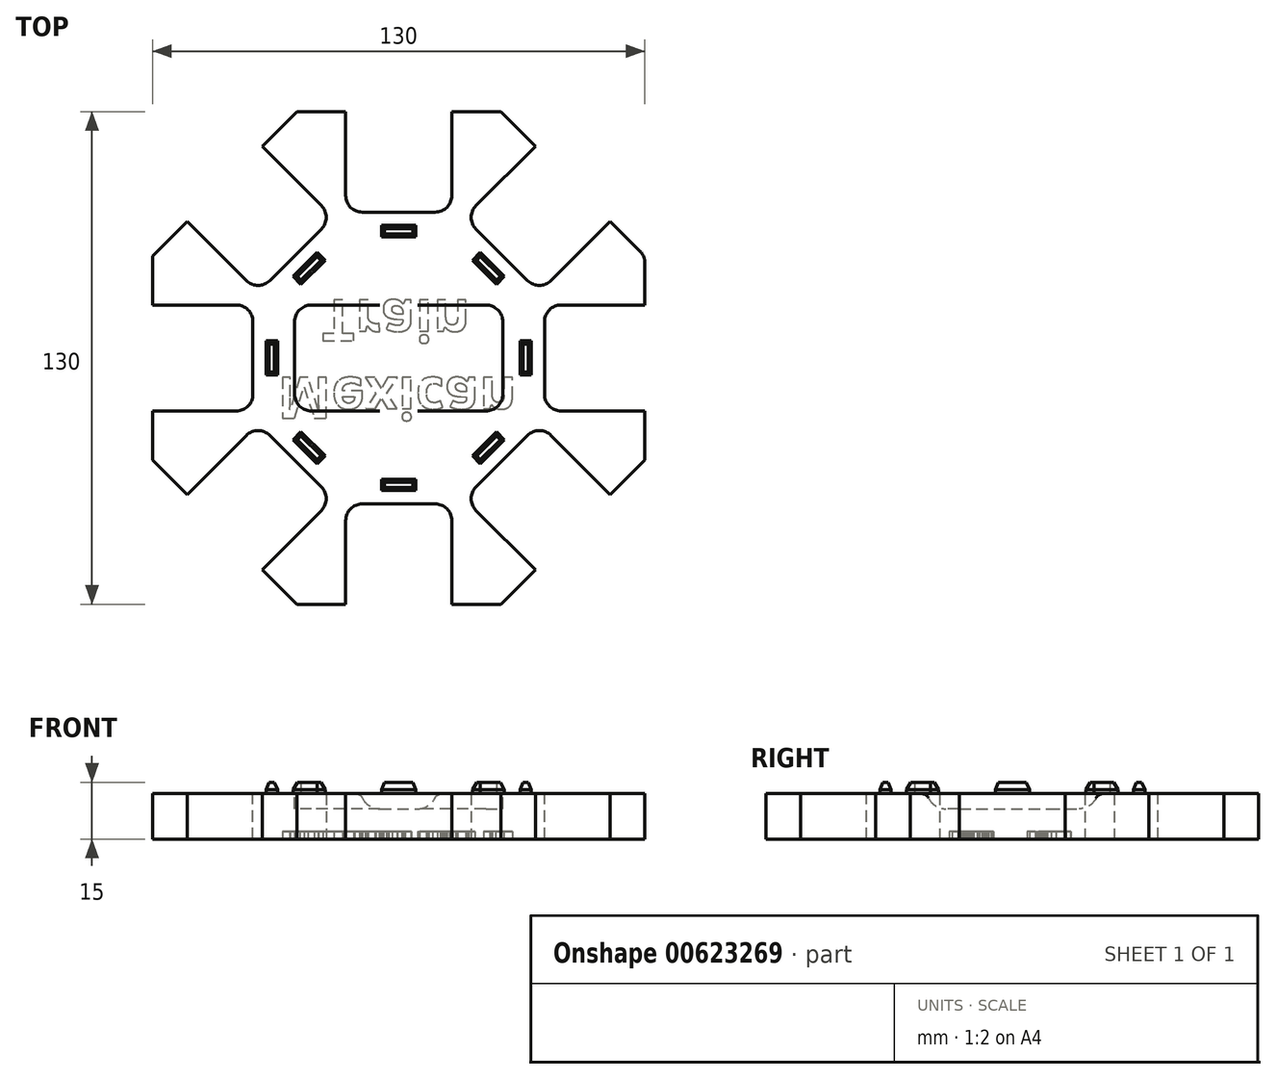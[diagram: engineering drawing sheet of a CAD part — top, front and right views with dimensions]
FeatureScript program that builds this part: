
annotation { "Feature Type Name" : "Feature", "Feature Type Description" : "" }
export const myFeature = defineFeature(function(context is Context, id is Id, definition is map)
    precondition{}
    {
        {
            var Q0;
            Q0=qCreatedBy(makeId("Top.planeOp"),FACE);
            var sketch = newSketch(context, id + "F0", { "sketchPlane" : qUnion([Q0])});
            skCircle(sketch, "E0.cCircle", {"center": v(0, 0) * mm, "radius": 65 * mm, "construction": true});
            skLineSegment(sketch, "E0.0", {"start": v(65, -26.92) * mm, "end": v(26.92, -65) * mm});
            skLineSegment(sketch, "E0.1", {"start": v(26.92, -65) * mm, "end": v(-26.92, -65) * mm});
            skLineSegment(sketch, "E0.2", {"start": v(-26.92, -65) * mm, "end": v(-65, -26.92) * mm});
            skLineSegment(sketch, "E0.3", {"start": v(-65, -26.92) * mm, "end": v(-65, 26.92) * mm});
            skLineSegment(sketch, "E0.4", {"start": v(-65, 26.92) * mm, "end": v(-26.92, 65) * mm});
            skLineSegment(sketch, "E0.5", {"start": v(-26.92, 65) * mm, "end": v(26.92, 65) * mm});
            skLineSegment(sketch, "E0.6", {"start": v(26.92, 65) * mm, "end": v(65, 26.92) * mm});
            skLineSegment(sketch, "E0.7", {"start": v(65, 26.92) * mm, "end": v(65, -26.92) * mm});
            skPoint(sketch, "E0.0.midPoint", {"position": v(45.96, -45.96) * mm});
            skLineSegment(sketch, "E1", {"start": v(0, 65) * mm, "end": v(0, 51.75) * mm, "construction": true});
            skLineSegment(sketch, "E2.bottom", {"start": v(-14, 65) * mm, "end": v(14, 65) * mm});
            skLineSegment(sketch, "E2.top", {"start": v(-14, 38.5) * mm, "end": v(14, 38.5) * mm});
            skLineSegment(sketch, "E2.left", {"start": v(-14, 65) * mm, "end": v(-14, 38.5) * mm});
            skLineSegment(sketch, "E2.right", {"start": v(14, 65) * mm, "end": v(14, 38.5) * mm});
            skPoint(sketch, "E2.middle", {"position": v(0, 51.75) * mm});
            skSolve(sketch);
        }
        {
            var Q0;
            Q0=makeQuery(id+"F0.imprint","IMPRINT",FACE,{"disambiguationData":[TD([[makeQuery(id+"F0.imprint","IMPRINT",EDGE,{"derivedFrom":sQuery(id+"F0.wireOp",EDGE,"E0.0")}),-1.0]])]});
            var Q1;
            Q1=makeQuery(id+"F0.imprint","IMPRINT",FACE,{"disambiguationData":[TD([[makeQuery(id+"F0.imprint","IMPRINT",EDGE,{"derivedFrom":sQuery(id+"F0.wireOp",EDGE,"E2.top")}),1.0]])]});
            extrude(context, id + "F1", {"entities" : qUnion([Q0, Q1]), "depth" : 12 * mm, "offsetDistance" : 25 * mm});
        }
        {
            var Q0;
            Q0=makeQuery(id+"F1.opExtrude","CAP_FACE",FACE,{"disambiguationData":[OSD([sQuery(id+"F0.wireOp",EDGE,"E0.0"),sQuery(id+"F0.wireOp",EDGE,"E0.1"),sQuery(id+"F0.wireOp",EDGE,"E0.2"),sQuery(id+"F0.wireOp",EDGE,"E0.3"),sQuery(id+"F0.wireOp",EDGE,"E0.4"),sQuery(id+"F0.wireOp",EDGE,"E0.5"),sQuery(id+"F0.wireOp",EDGE,"E0.6"),sQuery(id+"F0.wireOp",EDGE,"E0.7"),sQuery(id+"F0.wireOp",EDGE,"E2.bottom")])],"isStart":false});
            var sketch = newSketch(context, id + "F2", { "sketchPlane" : qUnion([Q0])});
            skLineSegment(sketch, "E3", {"start": v(0, 65) * mm, "end": v(0, 51.75) * mm, "construction": true});
            skLineSegment(sketch, "E4.bottom", {"start": v(14, 65) * mm, "end": v(-14, 65) * mm});
            skLineSegment(sketch, "E4.top", {"start": v(14, 38.5) * mm, "end": v(-14, 38.5) * mm});
            skLineSegment(sketch, "E4.left", {"start": v(14, 65) * mm, "end": v(14, 38.5) * mm});
            skLineSegment(sketch, "E4.right", {"start": v(-14, 65) * mm, "end": v(-14, 38.5) * mm});
            skPoint(sketch, "E4.middle", {"position": v(0, 51.75) * mm});
            skLineSegment(sketch, "E5.1.0", {"start": v(-55.86, 36.06) * mm, "end": v(-37.12, 17.32) * mm});
            skLineSegment(sketch, "E5.1.1", {"start": v(-36.06, 55.86) * mm, "end": v(-17.32, 37.12) * mm});
            skLineSegment(sketch, "E5.1.2", {"start": v(-17.32, 37.12) * mm, "end": v(-37.12, 17.32) * mm});
            skLineSegment(sketch, "E5.2.0", {"start": v(-65, -14) * mm, "end": v(-38.5, -14) * mm});
            skLineSegment(sketch, "E5.2.1", {"start": v(-65, 14) * mm, "end": v(-38.5, 14) * mm});
            skLineSegment(sketch, "E5.2.2", {"start": v(-38.5, 14) * mm, "end": v(-38.5, -14) * mm});
            skLineSegment(sketch, "E5.3.0", {"start": v(-36.06, -55.86) * mm, "end": v(-17.32, -37.12) * mm});
            skLineSegment(sketch, "E5.3.1", {"start": v(-55.86, -36.06) * mm, "end": v(-37.12, -17.32) * mm});
            skLineSegment(sketch, "E5.3.2", {"start": v(-37.12, -17.32) * mm, "end": v(-17.32, -37.12) * mm});
            skLineSegment(sketch, "E5.4.0", {"start": v(14, -65) * mm, "end": v(14, -38.5) * mm});
            skLineSegment(sketch, "E5.4.1", {"start": v(-14, -65) * mm, "end": v(-14, -38.5) * mm});
            skLineSegment(sketch, "E5.4.2", {"start": v(-14, -38.5) * mm, "end": v(14, -38.5) * mm});
            skLineSegment(sketch, "E5.5.0", {"start": v(55.86, -36.06) * mm, "end": v(37.12, -17.32) * mm});
            skLineSegment(sketch, "E5.5.1", {"start": v(36.06, -55.86) * mm, "end": v(17.32, -37.12) * mm});
            skLineSegment(sketch, "E5.5.2", {"start": v(17.32, -37.12) * mm, "end": v(37.12, -17.32) * mm});
            skLineSegment(sketch, "E5.6.0", {"start": v(65, 14) * mm, "end": v(38.5, 14) * mm});
            skLineSegment(sketch, "E5.6.1", {"start": v(65, -14) * mm, "end": v(38.5, -14) * mm});
            skLineSegment(sketch, "E5.6.2", {"start": v(38.5, -14) * mm, "end": v(38.5, 14) * mm});
            skLineSegment(sketch, "E5.7.0", {"start": v(36.06, 55.86) * mm, "end": v(17.32, 37.12) * mm});
            skLineSegment(sketch, "E5.7.1", {"start": v(55.86, 36.06) * mm, "end": v(37.12, 17.32) * mm});
            skLineSegment(sketch, "E5.7.2", {"start": v(37.12, 17.32) * mm, "end": v(17.32, 37.12) * mm});
            skPoint(sketch, "E5.center", {"position": v(0, 0) * mm});
            skLineSegment(sketch, "E6.bottom", {"start": v(27.5, -14) * mm, "end": v(-27.5, -14) * mm});
            skLineSegment(sketch, "E6.top", {"start": v(27.5, 14) * mm, "end": v(-27.5, 14) * mm});
            skLineSegment(sketch, "E6.left", {"start": v(27.5, -14) * mm, "end": v(27.5, 14) * mm});
            skLineSegment(sketch, "E6.right", {"start": v(-27.5, -14) * mm, "end": v(-27.5, 14) * mm});
            skLineSegment(sketch, "E7", {"start": v(0, 14) * mm, "end": v(0, -14) * mm});
            skSolve(sketch);
        }
        {
            var Q0;
            Q0=makeQuery(id+"F2.imprint","IMPRINT",FACE,{"disambiguationData":[TD([[makeQuery(id+"F2.imprint","IMPRINT",EDGE,{"derivedFrom":sQuery(id+"F2.wireOp",EDGE,"E4.bottom")}),-1.0]])]});
            var Q1;
            {var subQ0=sQuery(id+"F2.wireOp",EDGE,"E5.1.0");Q1=makeQuery(id+"F2.imprint","IMPRINT",FACE,{"disambiguationData":[TD([[makeQuery(id+"F2.imprint","IMPRINT",EDGE,{"derivedFrom":subQ0}),1.0]])]});}
            var Q2;
            {var subQ0=sQuery(id+"F2.wireOp",EDGE,"E5.2.0");Q2=makeQuery(id+"F2.imprint","IMPRINT",FACE,{"disambiguationData":[TD([[makeQuery(id+"F2.imprint","IMPRINT",EDGE,{"derivedFrom":subQ0}),1.0]])]});}
            var Q3;
            {var subQ0=sQuery(id+"F2.wireOp",EDGE,"E5.7.0");Q3=makeQuery(id+"F2.imprint","IMPRINT",FACE,{"disambiguationData":[TD([[makeQuery(id+"F2.imprint","IMPRINT",EDGE,{"derivedFrom":subQ0}),1.0]])]});}
            var Q4;
            {var subQ0=sQuery(id+"F2.wireOp",EDGE,"E5.6.0");Q4=makeQuery(id+"F2.imprint","IMPRINT",FACE,{"disambiguationData":[TD([[makeQuery(id+"F2.imprint","IMPRINT",EDGE,{"derivedFrom":subQ0}),1.0]])]});}
            var Q5;
            {var subQ0=sQuery(id+"F2.wireOp",EDGE,"E5.5.0");Q5=makeQuery(id+"F2.imprint","IMPRINT",FACE,{"disambiguationData":[TD([[makeQuery(id+"F2.imprint","IMPRINT",EDGE,{"derivedFrom":subQ0}),1.0]])]});}
            var Q6;
            {var subQ0=sQuery(id+"F2.wireOp",EDGE,"E5.4.0");Q6=makeQuery(id+"F2.imprint","IMPRINT",FACE,{"disambiguationData":[TD([[makeQuery(id+"F2.imprint","IMPRINT",EDGE,{"derivedFrom":subQ0}),1.0]])]});}
            var Q7;
            {var subQ0=sQuery(id+"F2.wireOp",EDGE,"E5.3.0");Q7=makeQuery(id+"F2.imprint","IMPRINT",FACE,{"disambiguationData":[TD([[makeQuery(id+"F2.imprint","IMPRINT",EDGE,{"derivedFrom":subQ0}),1.0]])]});}
            extrude(context, id + "F3", {"entities" : qUnion([Q0, Q1, Q2, Q3, Q4, Q5, Q6, Q7]), "operationType" : NewBodyOperationType.REMOVE, "oppositeDirection" : true, "depth" : 25 * mm, "offsetDistance" : 25 * mm});
        }
        {
            var Q0;
            Q0=makeQuery(id+"F3.boolean.opBoolean","COPY",EDGE,{"derivedFrom":makeQuery(id+"F3.opExtrude","SWEPT_EDGE",EDGE,{"disambiguationData":[OSD([sQuery(id+"F2.wireOp",EDGE,"E4.top"),sQuery(id+"F2.wireOp",EDGE,"E4.right")])]})});
            var Q1;
            Q1=makeQuery(id+"F3.boolean.opBoolean","COPY",EDGE,{"derivedFrom":makeQuery(id+"F3.opExtrude","SWEPT_EDGE",EDGE,{"disambiguationData":[OSD([sQuery(id+"F2.wireOp",EDGE,"E5.7.0"),sQuery(id+"F2.wireOp",EDGE,"E5.7.2")])]})});
            var Q2;
            Q2=makeQuery(id+"F3.boolean.opBoolean","COPY",EDGE,{"derivedFrom":makeQuery(id+"F3.opExtrude","SWEPT_EDGE",EDGE,{"disambiguationData":[OSD([sQuery(id+"F2.wireOp",EDGE,"E5.6.0"),sQuery(id+"F2.wireOp",EDGE,"E5.6.2")])]})});
            var Q3;
            Q3=makeQuery(id+"F3.boolean.opBoolean","COPY",EDGE,{"derivedFrom":makeQuery(id+"F3.opExtrude","SWEPT_EDGE",EDGE,{"disambiguationData":[OSD([sQuery(id+"F2.wireOp",EDGE,"E5.5.0"),sQuery(id+"F2.wireOp",EDGE,"E5.5.2")])]})});
            var Q4;
            Q4=makeQuery(id+"F3.boolean.opBoolean","COPY",EDGE,{"derivedFrom":makeQuery(id+"F3.opExtrude","SWEPT_EDGE",EDGE,{"disambiguationData":[OSD([sQuery(id+"F2.wireOp",EDGE,"E5.4.0"),sQuery(id+"F2.wireOp",EDGE,"E5.4.2")])]})});
            var Q5;
            Q5=makeQuery(id+"F3.boolean.opBoolean","COPY",EDGE,{"derivedFrom":makeQuery(id+"F3.opExtrude","SWEPT_EDGE",EDGE,{"disambiguationData":[OSD([sQuery(id+"F2.wireOp",EDGE,"E5.3.0"),sQuery(id+"F2.wireOp",EDGE,"E5.3.2")])]})});
            var Q6;
            Q6=makeQuery(id+"F3.boolean.opBoolean","COPY",EDGE,{"derivedFrom":makeQuery(id+"F3.opExtrude","SWEPT_EDGE",EDGE,{"disambiguationData":[OSD([sQuery(id+"F2.wireOp",EDGE,"E5.2.0"),sQuery(id+"F2.wireOp",EDGE,"E5.2.2")])]})});
            var Q7;
            Q7=makeQuery(id+"F3.boolean.opBoolean","COPY",EDGE,{"derivedFrom":makeQuery(id+"F3.opExtrude","SWEPT_EDGE",EDGE,{"disambiguationData":[OSD([sQuery(id+"F2.wireOp",EDGE,"E5.1.0"),sQuery(id+"F2.wireOp",EDGE,"E5.1.2")])]})});
            var Q8;
            Q8=makeQuery(id+"F3.boolean.opBoolean","COPY",EDGE,{"derivedFrom":makeQuery(id+"F3.opExtrude","SWEPT_EDGE",EDGE,{"disambiguationData":[OSD([sQuery(id+"F2.wireOp",EDGE,"E5.7.1"),sQuery(id+"F2.wireOp",EDGE,"E5.7.2")])]})});
            var Q9;
            Q9=makeQuery(id+"F1.opExtrude","SWEPT_EDGE",EDGE,{"disambiguationData":[OSD([sQuery(id+"F0.wireOp",EDGE,"E0.6"),sQuery(id+"F0.wireOp",EDGE,"E0.7")])]});
            var Q10;
            Q10=makeQuery(id+"F3.boolean.opBoolean","COPY",EDGE,{"derivedFrom":makeQuery(id+"F3.opExtrude","SWEPT_EDGE",EDGE,{"disambiguationData":[OSD([sQuery(id+"F2.wireOp",EDGE,"E5.6.1"),sQuery(id+"F2.wireOp",EDGE,"E5.6.2")])]})});
            var Q11;
            Q11=makeQuery(id+"F3.boolean.opBoolean","COPY",EDGE,{"derivedFrom":makeQuery(id+"F3.opExtrude","SWEPT_EDGE",EDGE,{"disambiguationData":[OSD([sQuery(id+"F2.wireOp",EDGE,"E5.5.1"),sQuery(id+"F2.wireOp",EDGE,"E5.5.2")])]})});
            var Q12;
            Q12=makeQuery(id+"F3.boolean.opBoolean","COPY",EDGE,{"derivedFrom":makeQuery(id+"F3.opExtrude","SWEPT_EDGE",EDGE,{"disambiguationData":[OSD([sQuery(id+"F2.wireOp",EDGE,"E5.4.1"),sQuery(id+"F2.wireOp",EDGE,"E5.4.2")])]})});
            var Q13;
            Q13=makeQuery(id+"F3.boolean.opBoolean","COPY",EDGE,{"derivedFrom":makeQuery(id+"F3.opExtrude","SWEPT_EDGE",EDGE,{"disambiguationData":[OSD([sQuery(id+"F2.wireOp",EDGE,"E5.3.1"),sQuery(id+"F2.wireOp",EDGE,"E5.3.2")])]})});
            var Q14;
            Q14=makeQuery(id+"F3.boolean.opBoolean","COPY",EDGE,{"derivedFrom":makeQuery(id+"F3.opExtrude","SWEPT_EDGE",EDGE,{"disambiguationData":[OSD([sQuery(id+"F2.wireOp",EDGE,"E5.2.1"),sQuery(id+"F2.wireOp",EDGE,"E5.2.2")])]})});
            var Q15;
            Q15=makeQuery(id+"F3.boolean.opBoolean","COPY",EDGE,{"derivedFrom":makeQuery(id+"F3.opExtrude","SWEPT_EDGE",EDGE,{"disambiguationData":[OSD([sQuery(id+"F2.wireOp",EDGE,"E5.1.1"),sQuery(id+"F2.wireOp",EDGE,"E5.1.2")])]})});
            var Q16;
            Q16=makeQuery(id+"F3.boolean.opBoolean","COPY",EDGE,{"derivedFrom":makeQuery(id+"F3.opExtrude","SWEPT_EDGE",EDGE,{"disambiguationData":[OSD([sQuery(id+"F2.wireOp",EDGE,"E4.top"),sQuery(id+"F2.wireOp",EDGE,"E4.left")])]})});
            fillet(context, id + "F4", {"entities" : qUnion([Q0, Q1, Q2, Q3, Q4, Q5, Q6, Q7, Q8, Q9, Q10, Q11, Q12, Q13, Q14, Q15, Q16]), "radius" : 4.4 * mm, "tangentPropagation" : true, "allowEdgeOverflow" : false});
        }
        {
            var Q0;
            Q0=makeQuery(id+"F2.imprint","IMPRINT",FACE,{"disambiguationData":[TD([[makeQuery(id+"F2.imprint","IMPRINT",EDGE,{"derivedFrom":sQuery(id+"F2.wireOp",EDGE,"E6.bottom")}),-1.0]])]});
            extrude(context, id + "F5", {"entities" : qUnion([Q0]), "operationType" : NewBodyOperationType.REMOVE, "oppositeDirection" : true, "depth" : 4 * mm, "offsetDistance" : 25 * mm});
        }
        {
            var Q0;
            Q0=makeQuery(id+"F1.opExtrude","CAP_FACE",FACE,{"disambiguationData":[OSD([sQuery(id+"F0.wireOp",EDGE,"E0.0"),sQuery(id+"F0.wireOp",EDGE,"E0.1"),sQuery(id+"F0.wireOp",EDGE,"E0.2"),sQuery(id+"F0.wireOp",EDGE,"E0.3"),sQuery(id+"F0.wireOp",EDGE,"E0.4"),sQuery(id+"F0.wireOp",EDGE,"E0.5"),sQuery(id+"F0.wireOp",EDGE,"E0.6"),sQuery(id+"F0.wireOp",EDGE,"E0.7")])],"isStart":false});
            var sketch = newSketch(context, id + "F6", { "sketchPlane" : qUnion([Q0])});
            skLineSegment(sketch, "E8", {"start": v(0, 38.5) * mm, "end": v(0, 33.5) * mm, "construction": true});
            skPoint(sketch, "E9.middle", {"position": v(0, 33.5) * mm});
            skLineSegment(sketch, "E10.bottom", {"start": v(4.5, 32) * mm, "end": v(-4.5, 32) * mm});
            skLineSegment(sketch, "E10.top", {"start": v(4.5, 35) * mm, "end": v(-4.5, 35) * mm});
            skLineSegment(sketch, "E10.left", {"start": v(4.5, 32) * mm, "end": v(4.5, 35) * mm});
            skLineSegment(sketch, "E10.right", {"start": v(-4.5, 32) * mm, "end": v(-4.5, 35) * mm});
            skSolve(sketch);
        }
        {
            var Q0;
            {var subQ0=sQuery(id+"F6.wireOp",EDGE,"E9.bottom");Q0=makeQuery(id+"F6.imprint","IMPRINT",FACE,{"disambiguationData":[TD([[makeQuery(id+"F6.imprint","IMPRINT",EDGE,{"derivedFrom":subQ0}),-1.0]])]});}
            var Q1;
            {var subQ5=sQuery(id+"F6.wireOp",EDGE,"E10.left");Q1=makeQuery(id+"F6.imprint","IMPRINT",FACE,{"disambiguationData":[TD([[makeQuery(id+"F6.imprint","IMPRINT",EDGE,{"derivedFrom":subQ5}),1.0]])]});}
            var Q2;
            {var subQ0=sQuery(id+"F6.wireOp",EDGE,"E10.bottom");var subQ1=sQuery(id+"F6.wireOp",EDGE,"E9.left");var subQ2=makeQuery(id+"F6.imprint","INTERSECT",VERTEX,{"derivedFrom":[subQ1,subQ0]});Q2=makeQuery(id+"F6.imprint","IMPRINT",FACE,{"disambiguationData":[TD([[makeQuery(id+"F6.imprint","IMPRINT",EDGE,{"disambiguationData":[TD([[subQ2,-1.0]])],"derivedFrom":subQ1}),1.0]])]});}
            var Q3;
            {var subQ0=sQuery(id+"F6.wireOp",EDGE,"E9.top");Q3=makeQuery(id+"F6.imprint","IMPRINT",FACE,{"disambiguationData":[TD([[makeQuery(id+"F6.imprint","IMPRINT",EDGE,{"derivedFrom":subQ0}),1.0]])]});}
            var Q4;
            {var subQ5=sQuery(id+"F6.wireOp",EDGE,"E10.right");Q4=makeQuery(id+"F6.imprint","IMPRINT",FACE,{"disambiguationData":[TD([[makeQuery(id+"F6.imprint","IMPRINT",EDGE,{"derivedFrom":subQ5}),-1.0]])]});}
            extrude(context, id + "F7", {"entities" : qUnion([Q0, Q1, Q2, Q3, Q4]), "depth" : 3 * mm, "offsetDistance" : 25 * mm});
        }
        {
            var Q0;
            Q0=makeQuery(id+"F1.opExtrude","CAP_FACE",FACE,{"disambiguationData":[OSD([sQuery(id+"F0.wireOp",EDGE,"E0.0"),sQuery(id+"F0.wireOp",EDGE,"E0.1"),sQuery(id+"F0.wireOp",EDGE,"E0.2"),sQuery(id+"F0.wireOp",EDGE,"E0.3"),sQuery(id+"F0.wireOp",EDGE,"E0.4"),sQuery(id+"F0.wireOp",EDGE,"E0.5"),sQuery(id+"F0.wireOp",EDGE,"E0.6"),sQuery(id+"F0.wireOp",EDGE,"E0.7")])],"isStart":false});
            var sketch = newSketch(context, id + "F8", { "sketchPlane" : qUnion([Q0])});
            skPoint(sketch, "E11", {"position": v(0, 0) * mm});
            skCircle(sketch, "E12", {"center": v(0, 0) * mm, "radius": 38.5 * mm, "construction": true});
            skSolve(sketch);
        }
        {
            var Q0;
            Q0=makeQuery(id+"F7.opExtrude","SWEPT_BODY",BODY,{"disambiguationData":[OSD([sQuery(id+"F6.wireOp",EDGE,"E9.bottom"),sQuery(id+"F6.wireOp",EDGE,"E9.top"),sQuery(id+"F6.wireOp",EDGE,"E9.left"),sQuery(id+"F6.wireOp",EDGE,"E9.right"),sQuery(id+"F6.wireOp",EDGE,"E10.bottom"),sQuery(id+"F6.wireOp",EDGE,"E10.top"),sQuery(id+"F6.wireOp",EDGE,"E10.left"),sQuery(id+"F6.wireOp",EDGE,"E10.right")])]});
            var Q1;
            Q1=sQuery(id+"F8.wireOp",EDGE,"E12");
            circularPattern(context, id + "F9", {"entities" : qUnion([Q0]), "axis" : qUnion([Q1]), "angle" : 360 * degree, "instanceCount" : 8, "equalSpace" : true});
        }
        {
            var Q0;
            Q0=makeQuery(id+"F1.opExtrude","CAP_FACE",FACE,{"disambiguationData":[OSD([sQuery(id+"F0.wireOp",EDGE,"E0.0"),sQuery(id+"F0.wireOp",EDGE,"E0.1"),sQuery(id+"F0.wireOp",EDGE,"E0.2"),sQuery(id+"F0.wireOp",EDGE,"E0.3"),sQuery(id+"F0.wireOp",EDGE,"E0.4"),sQuery(id+"F0.wireOp",EDGE,"E0.5"),sQuery(id+"F0.wireOp",EDGE,"E0.6"),sQuery(id+"F0.wireOp",EDGE,"E0.7")])],"isStart":true});
            var sketch = newSketch(context, id + "F10", { "sketchPlane" : qUnion([Q0])});
            skLineSegment(sketch, "E13", {"start": v(0, 0) * mm, "end": v(0, 16) * mm, "construction": true});
            skLineSegment(sketch, "E14", {"start": v(0, 0) * mm, "end": v(-32, 0) * mm, "construction": true});
            skText(sketch, "E15", { "text": "Mexican\n   Train\n", "fontName": "OpenSans-Bold.ttf"});
            const initialGuessF10  = {"E15": [-0.032, 0.00516, 1, 0, 0.01084]};
            skSetInitialGuess(sketch, initialGuessF10);
            skSolve(sketch);
        }
        {
            var Q0;
            Q0=qSketchRegion(id+"F10",true);
            extrude(context, id + "F11", {"entities" : qUnion([Q0]), "operationType" : NewBodyOperationType.REMOVE, "oppositeDirection" : true, "depth" : 2 * mm, "offsetDistance" : 25 * mm});
        }
        {
            var Q0;
            Q0=makeQuery(id+"F5.boolean.opBoolean","COPY",EDGE,{"derivedFrom":makeQuery(id+"F5.opExtrude","SWEPT_EDGE",EDGE,{"disambiguationData":[OSD([sQuery(id+"F2.wireOp",EDGE,"E6.top"),sQuery(id+"F2.wireOp",EDGE,"E6.right")])]})});
            var Q1;
            Q1=makeQuery(id+"F5.boolean.opBoolean","COPY",EDGE,{"derivedFrom":makeQuery(id+"F5.opExtrude","SWEPT_EDGE",EDGE,{"disambiguationData":[OSD([sQuery(id+"F2.wireOp",EDGE,"E6.bottom"),sQuery(id+"F2.wireOp",EDGE,"E6.right")])]})});
            var Q2;
            Q2=makeQuery(id+"F5.boolean.opBoolean","COPY",EDGE,{"derivedFrom":makeQuery(id+"F5.opExtrude","SWEPT_EDGE",EDGE,{"disambiguationData":[OSD([sQuery(id+"F2.wireOp",EDGE,"E6.bottom"),sQuery(id+"F2.wireOp",EDGE,"E6.left")])]})});
            var Q3;
            Q3=makeQuery(id+"F5.boolean.opBoolean","COPY",EDGE,{"derivedFrom":makeQuery(id+"F5.opExtrude","SWEPT_EDGE",EDGE,{"disambiguationData":[OSD([sQuery(id+"F2.wireOp",EDGE,"E6.top"),sQuery(id+"F2.wireOp",EDGE,"E6.left")])]})});
            fillet(context, id + "F12", {"entities" : qUnion([Q0, Q1, Q2, Q3]), "radius" : 4.5 * mm, "tangentPropagation" : true, "allowEdgeOverflow" : false});
        }
        {
            var Q0;
            Q0=makeQuery(id+"F9.opPattern","COPY",EDGE,{"derivedFrom":makeQuery(id+"F7.opExtrude","CAP_EDGE",EDGE,{"disambiguationData":[OSD([sQuery(id+"F6.wireOp",EDGE,"E10.right")])],"isStart":false}),"instanceName":"4"});
            var Q1;
            Q1=makeQuery(id+"F9.opPattern","COPY",EDGE,{"derivedFrom":makeQuery(id+"F7.opExtrude","CAP_EDGE",EDGE,{"disambiguationData":[OSD([sQuery(id+"F6.wireOp",EDGE,"E10.top")])],"isStart":false}),"instanceName":"4"});
            var Q2;
            Q2=makeQuery(id+"F9.opPattern","COPY",EDGE,{"derivedFrom":makeQuery(id+"F7.opExtrude","CAP_EDGE",EDGE,{"disambiguationData":[OSD([sQuery(id+"F6.wireOp",EDGE,"E10.bottom")])],"isStart":false}),"instanceName":"4"});
            var Q3;
            Q3=makeQuery(id+"F9.opPattern","COPY",FACE,{"derivedFrom":makeQuery(id+"F7.opExtrude","CAP_FACE",FACE,{"disambiguationData":[OSD([sQuery(id+"F6.wireOp",EDGE,"E10.bottom"),sQuery(id+"F6.wireOp",EDGE,"E10.top"),sQuery(id+"F6.wireOp",EDGE,"E10.left"),sQuery(id+"F6.wireOp",EDGE,"E10.right")])],"isStart":false}),"instanceName":"4"});
            chamfer(context, id + "F13", {"entities" : qUnion([Q0, Q1, Q2, Q3]), "chamferType" : ChamferType.TWO_OFFSETS, "width1" : 2 * mm, "oppositeDirection" : false, "width2" : .8 * mm, "tangentPropagation" : true});
        }
        {
            var Q0;
            Q0=makeQuery(id+"F9.opPattern","COPY",FACE,{"derivedFrom":makeQuery(id+"F7.opExtrude","CAP_FACE",FACE,{"disambiguationData":[OSD([sQuery(id+"F6.wireOp",EDGE,"E10.bottom"),sQuery(id+"F6.wireOp",EDGE,"E10.top"),sQuery(id+"F6.wireOp",EDGE,"E10.left"),sQuery(id+"F6.wireOp",EDGE,"E10.right")])],"isStart":false}),"instanceName":"5"});
            chamfer(context, id + "F14", {"entities" : qUnion([Q0]), "chamferType" : ChamferType.TWO_OFFSETS, "width1" : 2 * mm, "oppositeDirection" : false, "width2" : .8 * mm, "tangentPropagation" : true});
        }
        {
            var Q0;
            Q0=makeQuery(id+"F9.opPattern","COPY",FACE,{"derivedFrom":makeQuery(id+"F7.opExtrude","CAP_FACE",FACE,{"disambiguationData":[OSD([sQuery(id+"F6.wireOp",EDGE,"E10.bottom"),sQuery(id+"F6.wireOp",EDGE,"E10.top"),sQuery(id+"F6.wireOp",EDGE,"E10.left"),sQuery(id+"F6.wireOp",EDGE,"E10.right")])],"isStart":false}),"instanceName":"6"});
            chamfer(context, id + "F15", {"entities" : qUnion([Q0]), "chamferType" : ChamferType.TWO_OFFSETS, "width1" : 2 * mm, "oppositeDirection" : false, "width2" : .8 * mm, "tangentPropagation" : true});
        }
        {
            var Q0;
            Q0=makeQuery(id+"F9.opPattern","COPY",FACE,{"derivedFrom":makeQuery(id+"F7.opExtrude","CAP_FACE",FACE,{"disambiguationData":[OSD([sQuery(id+"F6.wireOp",EDGE,"E10.bottom"),sQuery(id+"F6.wireOp",EDGE,"E10.top"),sQuery(id+"F6.wireOp",EDGE,"E10.left"),sQuery(id+"F6.wireOp",EDGE,"E10.right")])],"isStart":false}),"instanceName":"7"});
            chamfer(context, id + "F16", {"entities" : qUnion([Q0]), "chamferType" : ChamferType.TWO_OFFSETS, "width1" : 2 * mm, "oppositeDirection" : false, "width2" : .8 * mm, "tangentPropagation" : true});
        }
        {
            var Q0;
            Q0=makeQuery(id+"F7.opExtrude","CAP_FACE",FACE,{"disambiguationData":[OSD([sQuery(id+"F6.wireOp",EDGE,"E10.bottom"),sQuery(id+"F6.wireOp",EDGE,"E10.top"),sQuery(id+"F6.wireOp",EDGE,"E10.left"),sQuery(id+"F6.wireOp",EDGE,"E10.right")])],"isStart":false});
            chamfer(context, id + "F17", {"entities" : qUnion([Q0]), "chamferType" : ChamferType.TWO_OFFSETS, "width1" : 2 * mm, "oppositeDirection" : false, "width2" : .8 * mm, "tangentPropagation" : true});
        }
        {
            var Q0;
            Q0=makeQuery(id+"F9.opPattern","COPY",FACE,{"derivedFrom":makeQuery(id+"F7.opExtrude","CAP_FACE",FACE,{"disambiguationData":[OSD([sQuery(id+"F6.wireOp",EDGE,"E10.bottom"),sQuery(id+"F6.wireOp",EDGE,"E10.top"),sQuery(id+"F6.wireOp",EDGE,"E10.left"),sQuery(id+"F6.wireOp",EDGE,"E10.right")])],"isStart":false}),"instanceName":"1"});
            chamfer(context, id + "F18", {"entities" : qUnion([Q0]), "chamferType" : ChamferType.TWO_OFFSETS, "width1" : 2 * mm, "oppositeDirection" : false, "width2" : .8 * mm, "tangentPropagation" : true});
        }
        {
            var Q0;
            Q0=makeQuery(id+"F9.opPattern","COPY",FACE,{"derivedFrom":makeQuery(id+"F7.opExtrude","CAP_FACE",FACE,{"disambiguationData":[OSD([sQuery(id+"F6.wireOp",EDGE,"E10.bottom"),sQuery(id+"F6.wireOp",EDGE,"E10.top"),sQuery(id+"F6.wireOp",EDGE,"E10.left"),sQuery(id+"F6.wireOp",EDGE,"E10.right")])],"isStart":false}),"instanceName":"2"});
            chamfer(context, id + "F19", {"entities" : qUnion([Q0]), "chamferType" : ChamferType.TWO_OFFSETS, "width1" : 2 * mm, "oppositeDirection" : false, "width2" : .8 * mm, "tangentPropagation" : true});
        }
        {
            var Q0;
            Q0=makeQuery(id+"F9.opPattern","COPY",FACE,{"derivedFrom":makeQuery(id+"F7.opExtrude","CAP_FACE",FACE,{"disambiguationData":[OSD([sQuery(id+"F6.wireOp",EDGE,"E10.bottom"),sQuery(id+"F6.wireOp",EDGE,"E10.top"),sQuery(id+"F6.wireOp",EDGE,"E10.left"),sQuery(id+"F6.wireOp",EDGE,"E10.right")])],"isStart":false}),"instanceName":"3"});
            chamfer(context, id + "F20", {"entities" : qUnion([Q0]), "chamferType" : ChamferType.TWO_OFFSETS, "width1" : 2 * mm, "oppositeDirection" : false, "width2" : .8 * mm, "tangentPropagation" : true});
        }
        {
            var Q0;
            Q0=makeQuery(id+"F1.opExtrude","CAP_FACE",FACE,{"disambiguationData":[OSD([sQuery(id+"F0.wireOp",EDGE,"E0.0"),sQuery(id+"F0.wireOp",EDGE,"E0.1"),sQuery(id+"F0.wireOp",EDGE,"E0.2"),sQuery(id+"F0.wireOp",EDGE,"E0.3"),sQuery(id+"F0.wireOp",EDGE,"E0.4"),sQuery(id+"F0.wireOp",EDGE,"E0.5"),sQuery(id+"F0.wireOp",EDGE,"E0.6"),sQuery(id+"F0.wireOp",EDGE,"E0.7")])],"isStart":false});
            var sketch = newSketch(context, id + "F21", { "sketchPlane" : qUnion([Q0])});
            skLineSegment(sketch, "E16.bottom", {"start": v(10, -22.5) * mm, "end": v(-10, -22.5) * mm});
            skLineSegment(sketch, "E16.top", {"start": v(10, 22.5) * mm, "end": v(-10, 22.5) * mm});
            skLineSegment(sketch, "E16.left", {"start": v(10, -22.5) * mm, "end": v(10, 22.5) * mm});
            skLineSegment(sketch, "E16.right", {"start": v(-10, -22.5) * mm, "end": v(-10, 22.5) * mm});
            skPoint(sketch, "E16.middle", {"position": v(0, 0) * mm});
            skArc(sketch, "E17", {"start": v(10, 14) * mm, "mid": v(0, 22.5) * mm, "end": v(-10, 14) * mm});
            skArc(sketch, "E18", {"start": v(-10, -14) * mm, "mid": v(0, -22.5) * mm, "end": v(10, -14) * mm});
            skSolve(sketch);
        }
        {
            var Q0;
            {var subQ0=sQuery(id+"F21.wireOp",EDGE,"E17");var subQ3=makeQuery(id+"F21.imprint","INTERSECT",VERTEX,{"derivedFrom":[sQuery(id+"F21.wireOp",EDGE,"E16.top"),subQ0]});Q0=makeQuery(id+"F21.imprint","IMPRINT",FACE,{"disambiguationData":[TD([[makeQuery(id+"F21.imprint","IMPRINT",EDGE,{"disambiguationData":[TD([[subQ3,1.0]])],"derivedFrom":subQ0}),1.0]])]});}
            var Q1;
            {var subQ0=sQuery(id+"F21.wireOp",EDGE,"E18");var subQ3=makeQuery(id+"F21.imprint","INTERSECT",VERTEX,{"derivedFrom":[sQuery(id+"F21.wireOp",EDGE,"E16.bottom"),subQ0]});Q1=makeQuery(id+"F21.imprint","IMPRINT",FACE,{"disambiguationData":[TD([[makeQuery(id+"F21.imprint","IMPRINT",EDGE,{"disambiguationData":[TD([[subQ3,1.0]])],"derivedFrom":subQ0}),1.0]])]});}
            extrude(context, id + "F22", {"entities" : qUnion([Q0, Q1]), "operationType" : NewBodyOperationType.REMOVE, "oppositeDirection" : true, "depth" : 4 * mm, "offsetDistance" : 25 * mm});
        }
        {
            var Q0;
            Q0=makeQuery(id+"F22.boolean.opBoolean","COPY",EDGE,{"derivedFrom":makeQuery(id+"F22.opExtrude","CAP_EDGE",EDGE,{"disambiguationData":[OSD([sQuery(id+"F21.wireOp",EDGE,"E17")])],"isStart":false})});
            var Q1;
            Q1=makeQuery(id+"F22.boolean.opBoolean","COPY",EDGE,{"derivedFrom":makeQuery(id+"F22.opExtrude","CAP_EDGE",EDGE,{"disambiguationData":[OSD([sQuery(id+"F21.wireOp",EDGE,"E18")])],"isStart":false})});
            fillet(context, id + "F23", {"entities" : qUnion([Q0, Q1]), "radius" : 5 * mm, "tangentPropagation" : true, "allowEdgeOverflow" : false});
        }
        {
            var Q0;
            Q0=makeQuery(id+"F23.opFillet","BLEND_EDGE",EDGE,{"blendedFrom":[makeQuery(id+"F22.boolean.opBoolean","COPY",EDGE,{"derivedFrom":makeQuery(id+"F22.opExtrude","CAP_EDGE",EDGE,{"disambiguationData":[OSD([sQuery(id+"F21.wireOp",EDGE,"E18")])],"isStart":false})}),makeQuery(id+"F1.opExtrude","CAP_FACE",FACE,{"disambiguationData":[OSD([sQuery(id+"F0.wireOp",EDGE,"E0.0"),sQuery(id+"F0.wireOp",EDGE,"E0.1"),sQuery(id+"F0.wireOp",EDGE,"E0.2"),sQuery(id+"F0.wireOp",EDGE,"E0.3"),sQuery(id+"F0.wireOp",EDGE,"E0.4"),sQuery(id+"F0.wireOp",EDGE,"E0.5"),sQuery(id+"F0.wireOp",EDGE,"E0.6"),sQuery(id+"F0.wireOp",EDGE,"E0.7")])],"isStart":false})],"blendedInto":[makeQuery(id+"F1.opExtrude","CAP_FACE",FACE,{"disambiguationData":[OSD([sQuery(id+"F0.wireOp",EDGE,"E0.0"),sQuery(id+"F0.wireOp",EDGE,"E0.1"),sQuery(id+"F0.wireOp",EDGE,"E0.2"),sQuery(id+"F0.wireOp",EDGE,"E0.3"),sQuery(id+"F0.wireOp",EDGE,"E0.4"),sQuery(id+"F0.wireOp",EDGE,"E0.5"),sQuery(id+"F0.wireOp",EDGE,"E0.6"),sQuery(id+"F0.wireOp",EDGE,"E0.7")])],"isStart":false})]});
            var Q1;
            Q1=makeQuery(id+"F23.opFillet","BLEND_EDGE",EDGE,{"blendedFrom":[makeQuery(id+"F22.boolean.opBoolean","COPY",EDGE,{"derivedFrom":makeQuery(id+"F22.opExtrude","CAP_EDGE",EDGE,{"disambiguationData":[OSD([sQuery(id+"F21.wireOp",EDGE,"E17")])],"isStart":false})}),makeQuery(id+"F1.opExtrude","CAP_FACE",FACE,{"disambiguationData":[OSD([sQuery(id+"F0.wireOp",EDGE,"E0.0"),sQuery(id+"F0.wireOp",EDGE,"E0.1"),sQuery(id+"F0.wireOp",EDGE,"E0.2"),sQuery(id+"F0.wireOp",EDGE,"E0.3"),sQuery(id+"F0.wireOp",EDGE,"E0.4"),sQuery(id+"F0.wireOp",EDGE,"E0.5"),sQuery(id+"F0.wireOp",EDGE,"E0.6"),sQuery(id+"F0.wireOp",EDGE,"E0.7")])],"isStart":false})],"blendedInto":[makeQuery(id+"F1.opExtrude","CAP_FACE",FACE,{"disambiguationData":[OSD([sQuery(id+"F0.wireOp",EDGE,"E0.0"),sQuery(id+"F0.wireOp",EDGE,"E0.1"),sQuery(id+"F0.wireOp",EDGE,"E0.2"),sQuery(id+"F0.wireOp",EDGE,"E0.3"),sQuery(id+"F0.wireOp",EDGE,"E0.4"),sQuery(id+"F0.wireOp",EDGE,"E0.5"),sQuery(id+"F0.wireOp",EDGE,"E0.6"),sQuery(id+"F0.wireOp",EDGE,"E0.7")])],"isStart":false})]});
            fillet(context, id + "F24", {"entities" : qUnion([Q0, Q1]), "radius" : 2 * mm, "tangentPropagation" : true, "allowEdgeOverflow" : false});
        }
    });
